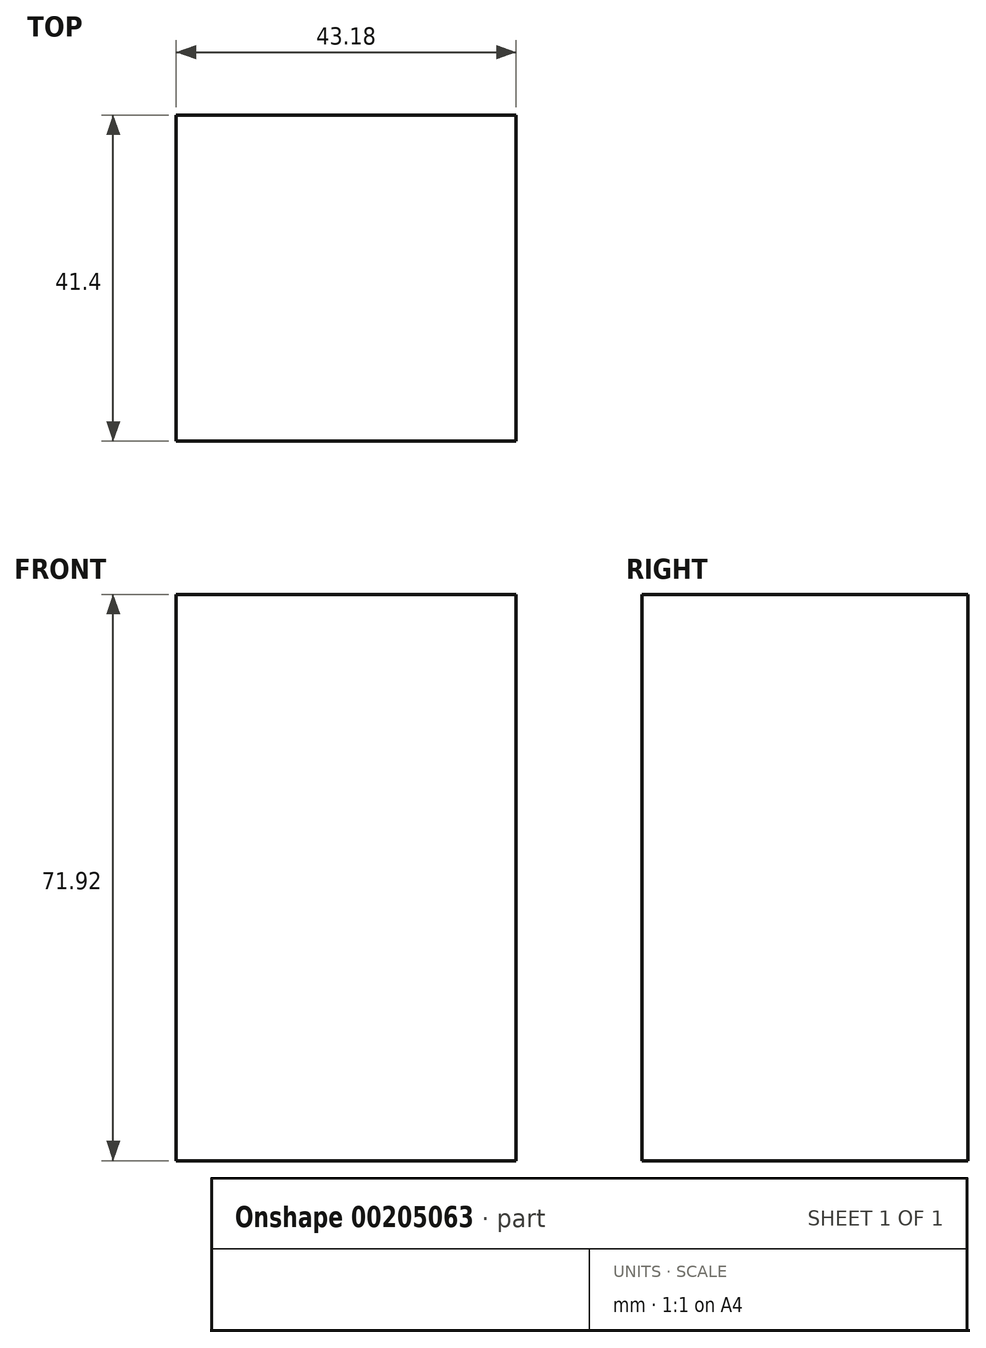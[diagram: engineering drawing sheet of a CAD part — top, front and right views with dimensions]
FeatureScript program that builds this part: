
annotation { "Feature Type Name" : "Feature", "Feature Type Description" : "" }
export const myFeature = defineFeature(function(context is Context, id is Id, definition is map)
    precondition{}
    {
        {
            var Q0;
            Q0=qCreatedBy(makeId("Right.planeOp"),FACE);
            var sketch = newSketch(context, id + "F0", { "sketchPlane" : qUnion([Q0])});
            skLineSegment(sketch, "E0.bottom", {"start": v(20.7, -35.96) * mm, "end": v(-20.7, -35.96) * mm});
            skLineSegment(sketch, "E0.top", {"start": v(20.7, 35.96) * mm, "end": v(-20.7, 35.96) * mm});
            skLineSegment(sketch, "E0.left", {"start": v(20.7, -35.96) * mm, "end": v(20.7, 35.96) * mm});
            skLineSegment(sketch, "E0.right", {"start": v(-20.7, -35.96) * mm, "end": v(-20.7, 35.96) * mm});
            skPoint(sketch, "E0.middle", {"position": v(0, 0) * mm});
            skSolve(sketch);
        }
        {
            var Q0;
            Q0=makeQuery(id+"F0.imprint","IMPRINT",FACE,{"disambiguationData":[TD([[makeQuery(id+"F0.imprint","IMPRINT",EDGE,{"derivedFrom":sQuery(id+"F0.wireOp",EDGE,"E0.bottom")}),-1.0]])]});
            extrude(context, id + "F1", {"entities" : qUnion([Q0]), "endBound" : BoundingType.SYMMETRIC, "depth" : 43.18 * mm});
        }
    });
